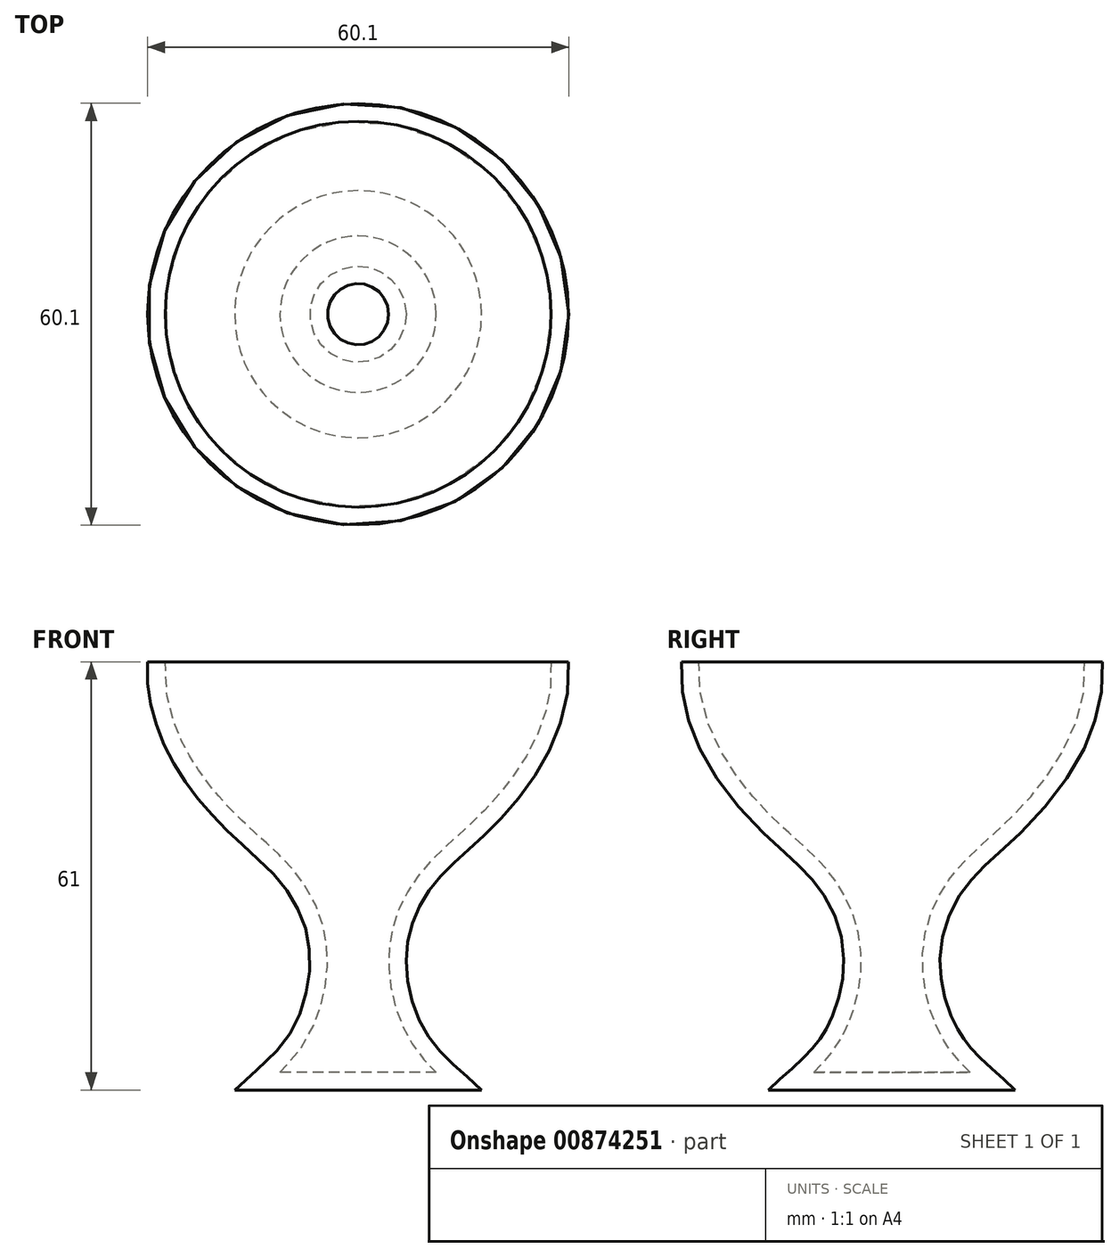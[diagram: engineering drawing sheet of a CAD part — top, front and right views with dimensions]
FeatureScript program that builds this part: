
annotation { "Feature Type Name" : "Feature", "Feature Type Description" : "" }
export const myFeature = defineFeature(function(context is Context, id is Id, definition is map)
    precondition{}
    {
        {
            var Q0;
            Q0=qCreatedBy(makeId("Front.planeOp"),FACE);
            var sketch = newSketch(context, id + "F0", { "sketchPlane" : qUnion([Q0])});
            skLineSegment(sketch, "E0", {"start": v(0, 31.74) * mm, "end": v(30, 31.74) * mm});
            skFitSpline(sketch, "E1", {"points": [v(30, 31.74) * mm, v(20.04, 9.08) * mm, v(10.75, 0) * mm, v(6.9, -9.8) * mm, v(9.93, -21.5) * mm, v(17.6, -29.26) * mm], "startDerivative": vector(7.1, -105.3) * mm, "endDerivative": vector(46.84, -45.34) * mm});
            skLineSegment(sketch, "E2", {"start": v(17.6, -29.26) * mm, "end": v(0, -29.26) * mm});
            skLineSegment(sketch, "E3", {"start": v(0, 31.74) * mm, "end": v(0, -29.26) * mm});
            skLineSegment(sketch, "E4", {"start": v(0, 25.69) * mm, "end": v(0, -36.03) * mm, "construction": true});
            skSolve(sketch);
        }
        {
            var Q0;
            Q0=qSketchRegion(id+"F0",true);
            var Q1;
            Q1=sQuery(id+"F0.wireOp",EDGE,"E3");
            revolve(context, id + "F1", {"surfaceOperationType" : NewSurfaceOperationType.NEW, "entities" : qUnion([Q0]), "axis" : qUnion([Q1]), "revolveType" : RevolveType.FULL});
        }
        {
            var Q0;
            Q0=makeQuery(id+"F1.opRevolve","SWEPT_FACE",FACE,{"disambiguationData":[OSD([sQuery(id+"F0.wireOp",EDGE,"E0")])]});
            shell(context, id + "F2", {"entities" : qUnion([Q0]), "thickness" : 2.5 * mm});
        }
    });
